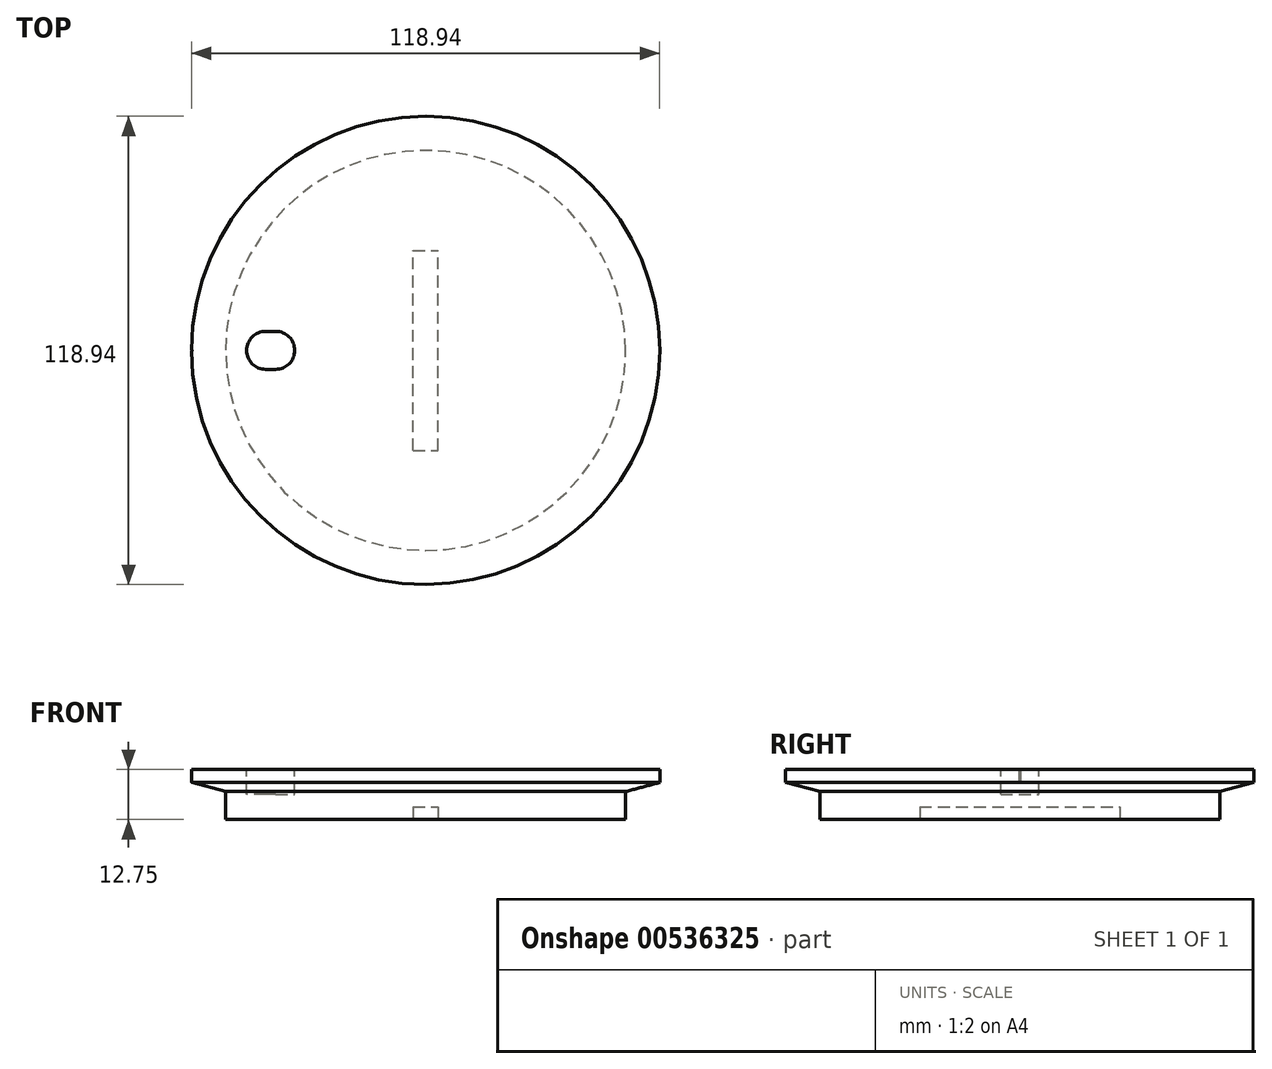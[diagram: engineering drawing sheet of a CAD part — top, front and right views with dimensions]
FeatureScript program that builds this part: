
annotation { "Feature Type Name" : "Feature", "Feature Type Description" : "" }
export const myFeature = defineFeature(function(context is Context, id is Id, definition is map)
    precondition{}
    {
        {
            var Q0;
            Q0=qCreatedBy(makeId("Front.planeOp"),FACE);
            var sketch = newSketch(context, id + "F0", { "sketchPlane" : qUnion([Q0])});
            skLineSegment(sketch, "E0", {"start": v(0, 0) * mm, "end": v(0, 85.37) * mm, "construction": true});
            skLineSegment(sketch, "E1", {"start": v(0, 0) * mm, "end": v(0, -83.14) * mm, "construction": true});
            skLineSegment(sketch, "E2", {"start": v(0, 0) * mm, "end": v(59.47, 0) * mm});
            skLineSegment(sketch, "E3", {"start": v(59.47, 0) * mm, "end": v(59.47, -3.3) * mm});
            skLineSegment(sketch, "E4", {"start": v(59.47, -3.3) * mm, "end": v(50.8, -5.63) * mm});
            skLineSegment(sketch, "E5", {"start": v(0, 0) * mm, "end": v(0, -12.75) * mm});
            skLineSegment(sketch, "E6", {"start": v(0, -12.75) * mm, "end": v(50.8, -12.75) * mm});
            skLineSegment(sketch, "E7", {"start": v(50.8, -12.75) * mm, "end": v(50.8, -5.63) * mm});
            skSolve(sketch);
        }
        {
            var Q0;
            Q0=makeQuery(id+"F0.imprint","IMPRINT",FACE,{"disambiguationData":[TD([[makeQuery(id+"F0.imprint","IMPRINT",EDGE,{"derivedFrom":sQuery(id+"F0.wireOp",EDGE,"E2")}),-1.0]])]});
            var Q1;
            Q1=sQuery(id+"F0.wireOp",EDGE,"E5");
            revolve(context, id + "F1", {"entities" : qUnion([Q0]), "axis" : qUnion([Q1]), "revolveType" : RevolveType.FULL});
        }
        {
            var Q0;
            Q0=makeQuery(id+"F1.opRevolve","SWEPT_FACE",FACE,{"disambiguationData":[OSD([sQuery(id+"F0.wireOp",EDGE,"E2")])]});
            var sketch = newSketch(context, id + "F2", { "sketchPlane" : qUnion([Q0])});
            skLineSegment(sketch, "E8", {"start": v(-38.1, -4.83) * mm, "end": v(-40.64, -4.83) * mm});
            skLineSegment(sketch, "E9", {"start": v(-40.64, 4.83) * mm, "end": v(-38.1, 4.83) * mm});
            skArc(sketch, "E10", {"start": v(-38.1, -4.83) * mm, "mid": v(-33.27, 0) * mm, "end": v(-38.1, 4.83) * mm});
            skArc(sketch, "E11", {"start": v(-40.64, 4.83) * mm, "mid": v(-45.47, 0) * mm, "end": v(-40.64, -4.83) * mm});
            skPoint(sketch, "E12.orphan", {"position": v(-38.1, 4.83) * mm});
            skPoint(sketch, "E13.orphan", {"position": v(-38.1, -4.83) * mm});
            skPoint(sketch, "E14.start.orphan", {"position": v(0, 4.83) * mm});
            skSolve(sketch);
        }
        {
            var Q0;
            Q0 = qSketchRegion(id + "F2", true);
            extrude(context, id + "F3", {"entities" : qUnion([Q0]), "operationType" : NewBodyOperationType.REMOVE, "oppositeDirection" : true, "depth" : 6.35 * mm, "offsetDistance" : 25.4 * mm});
        }
        {
            var Q0;
            Q0=makeQuery(id+"F1.opRevolve","SWEPT_FACE",FACE,{"disambiguationData":[OSD([sQuery(id+"F0.wireOp",EDGE,"E2")])]});
            var sketch = newSketch(context, id + "F4", { "sketchPlane" : qUnion([Q0])});
            skLineSegment(sketch, "E15.0", {"start": v(-59.35, 0.13) * mm, "end": v(-59.47, 0.13) * mm});
            skLineSegment(sketch, "E16.0", {"start": v(-59.35, -0.13) * mm, "end": v(-59.47, -0.13) * mm});
            skArc(sketch, "E17.0", {"start": v(-59.35, 0.13) * mm, "mid": v(-59.35, 0) * mm, "end": v(-59.35, -0.13) * mm});
            skLineSegment(sketch, "E18", {"start": v(-59.47, -0.13) * mm, "end": v(-59.47, 0.13) * mm});
            skPoint(sketch, "E19.start.orphan", {"position": v(-40.64, 0) * mm});
            skSolve(sketch);
        }
        {
            var Q0;
            Q0 = qSketchRegion(id + "F4", true);
            extrude(context, id + "F5", {"entities" : qUnion([Q0]), "operationType" : NewBodyOperationType.REMOVE, "oppositeDirection" : true, "depth" : 25.4 * mm, "offsetDistance" : 25.4 * mm});
        }
        {
            var Q0;
            Q0=makeQuery(id+"F1.opRevolve","SWEPT_FACE",FACE,{"disambiguationData":[OSD([sQuery(id+"F0.wireOp",EDGE,"E6")])]});
            var sketch = newSketch(context, id + "F6", { "sketchPlane" : qUnion([Q0])});
            skLineSegment(sketch, "E20.0", {"start": v(3.18, 0) * mm, "end": v(3.18, 25.4) * mm});
            skLineSegment(sketch, "E21.0", {"start": v(-3.18, 0) * mm, "end": v(-3.18, 25.4) * mm});
            skLineSegment(sketch, "E22.0", {"start": v(-3.18, 0) * mm, "end": v(-3.17, -25.4) * mm});
            skLineSegment(sketch, "E23.0", {"start": v(3.17, 0) * mm, "end": v(3.18, -25.4) * mm});
            skLineSegment(sketch, "E24", {"start": v(-3.17, -25.4) * mm, "end": v(3.18, -25.4) * mm});
            skLineSegment(sketch, "E25", {"start": v(-3.18, 25.4) * mm, "end": v(3.18, 25.4) * mm});
            skSolve(sketch);
        }
        {
            var Q0;
            Q0=makeQuery(id+"F6.imprint","IMPRINT",FACE,{"disambiguationData":[TD([[makeQuery(id+"F6.imprint","IMPRINT",EDGE,{"derivedFrom":sQuery(id+"F6.wireOp",EDGE,"E20.0")}),1.0]])]});
            extrude(context, id + "F7", {"entities" : qUnion([Q0]), "operationType" : NewBodyOperationType.REMOVE, "oppositeDirection" : true, "depth" : 3.17 * mm, "offsetDistance" : 25.4 * mm});
        }
    });
